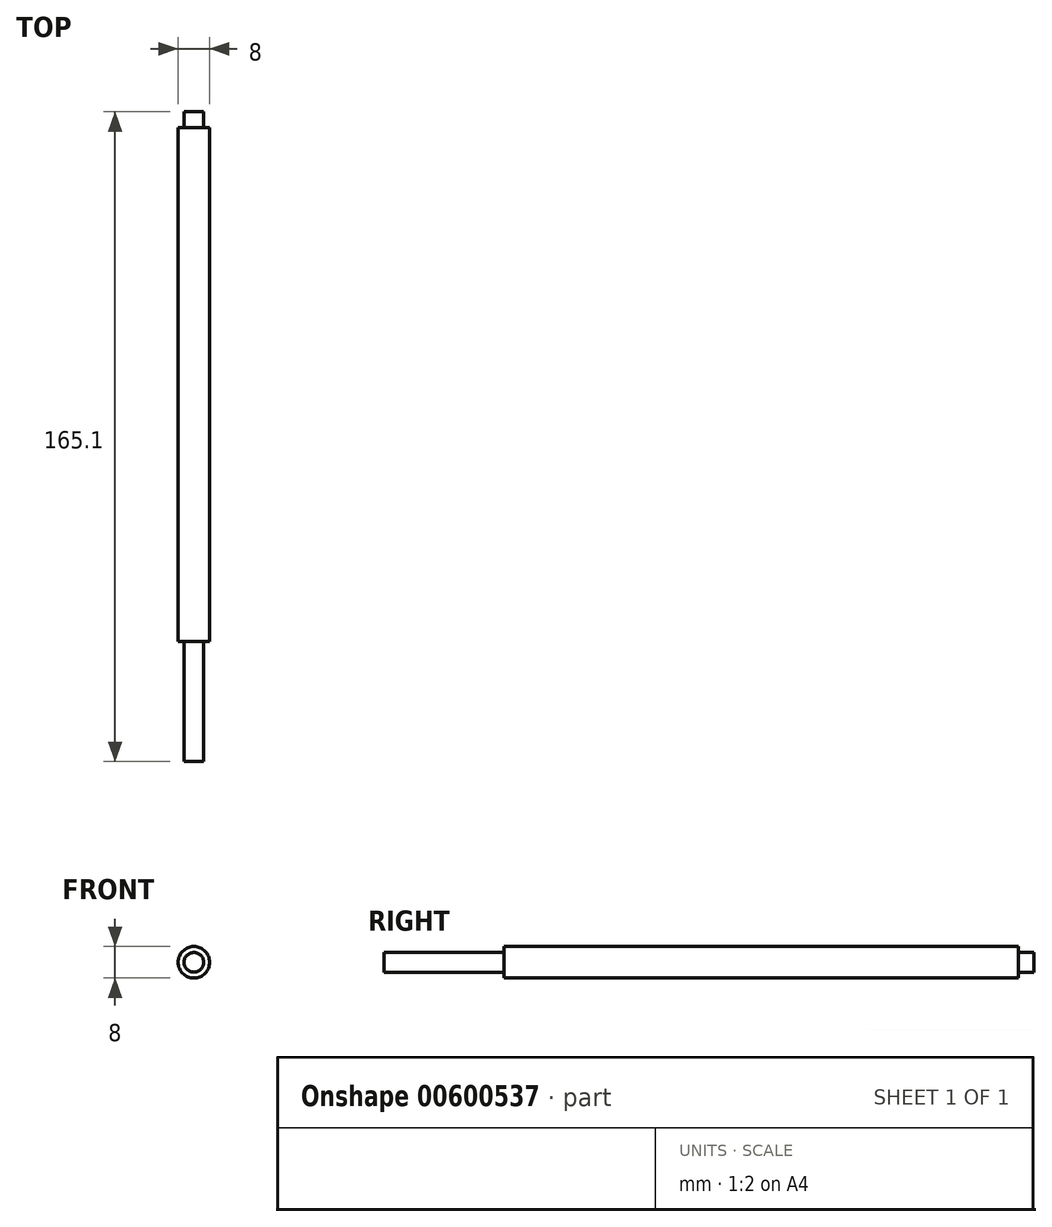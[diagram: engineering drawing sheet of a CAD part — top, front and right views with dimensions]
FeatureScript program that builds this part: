
annotation { "Feature Type Name" : "Feature", "Feature Type Description" : "" }
export const myFeature = defineFeature(function(context is Context, id is Id, definition is map)
    precondition{}
    {
        {
            var Q0;
            Q0=qCreatedBy(makeId("Front.planeOp"),FACE);
            var sketch = newSketch(context, id + "F0", { "sketchPlane" : qUnion([Q0])});
            skCircle(sketch, "E0", {"center": v(0, 0) * mm, "radius": 4 * mm});
            skSolve(sketch);
        }
        {
            var Q0;
            Q0=makeQuery(id+"F0.imprint","IMPRINT",FACE,{"disambiguationData":[TD([[makeQuery(id+"F0.imprint","IMPRINT",EDGE,{"derivedFrom":sQuery(id+"F0.wireOp",EDGE,"E0")}),1.0]])]});
            extrude(context, id + "F1", {"entities" : qUnion([Q0]), "depth" : 134.62 * mm, "offsetDistance" : 25.4 * mm});
        }
        {
            var Q0;
            Q0=makeQuery(id+"F1.opExtrude","CAP_FACE",FACE,{"disambiguationData":[OSD([sQuery(id+"F0.wireOp",EDGE,"E0")])],"isStart":true});
            var sketch = newSketch(context, id + "F2", { "sketchPlane" : qUnion([Q0])});
            skCircle(sketch, "E1", {"center": v(0, 0) * mm, "radius": 2.5 * mm});
            skSolve(sketch);
        }
        {
            var Q0;
            Q0=makeQuery(id+"F2.imprint","IMPRINT",FACE,{"disambiguationData":[TD([[makeQuery(id+"F2.imprint","IMPRINT",EDGE,{"derivedFrom":sQuery(id+"F2.wireOp",EDGE,"E1")}),-1.0]])]});
            extrude(context, id + "F3", {"entities" : qUnion([Q0]), "operationType" : NewBodyOperationType.REMOVE, "oppositeDirection" : true, "depth" : 4 * mm, "offsetDistance" : 25.4 * mm});
        }
        {
            var Q0;
            Q0=makeQuery(id+"F1.opExtrude","CAP_FACE",FACE,{"disambiguationData":[OSD([sQuery(id+"F0.wireOp",EDGE,"E0")])],"isStart":false});
            var sketch = newSketch(context, id + "F4", { "sketchPlane" : qUnion([Q0])});
            skCircle(sketch, "E2", {"center": v(0, 0) * mm, "radius": 2.5 * mm});
            skSolve(sketch);
        }
        {
            var Q0;
            Q0=makeQuery(id+"F4.imprint","IMPRINT",FACE,{"disambiguationData":[TD([[makeQuery(id+"F4.imprint","IMPRINT",EDGE,{"derivedFrom":sQuery(id+"F4.wireOp",EDGE,"E2")}),1.0]])]});
            extrude(context, id + "F5", {"entities" : qUnion([Q0]), "operationType" : NewBodyOperationType.ADD, "depth" : 30.48 * mm, "offsetDistance" : 25.4 * mm});
        }
    });
